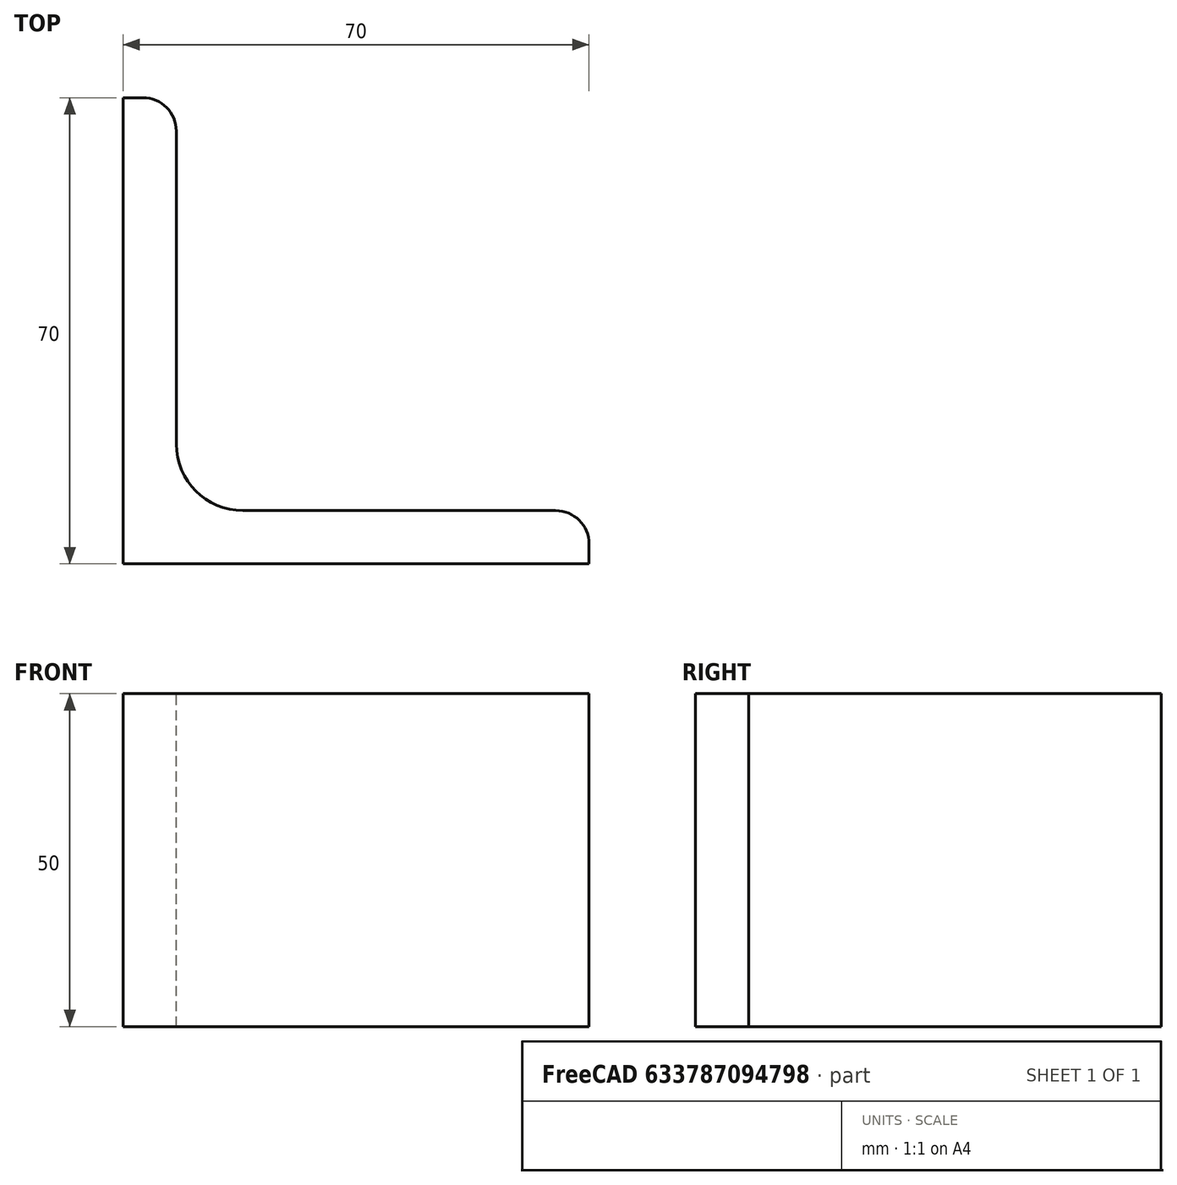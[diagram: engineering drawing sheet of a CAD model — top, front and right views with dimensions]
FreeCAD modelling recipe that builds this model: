
FCSTD DOCUMENT  (FreeCAD 0.15R4671 (Git))
Label: Angle Bar L70x70x8 EN10056 S235JR
License: All rights reserved
LicenseURL: http://en.wikipedia.org/wiki/All_rights_reserved
objects: Sketcher::SketchObject×1, Part::Extrusion×1
note: 2 computed .brp shape members not serialized (recipe doc carries the construction recipe); baked Part::Feature solids carry a one-line shape summary decoded from their .brp

FEATURE [Sketcher::SketchObject] Sketch
  sketch-geometry (9):
    g0: LineSegment StartX=0 StartY=0 StartZ=0 EndX=70 EndY=0 EndZ=0
    g1: LineSegment StartX=70 StartY=0 StartZ=0 EndX=70 EndY=3 EndZ=0
    g2: LineSegment StartX=65 StartY=8 StartZ=0 EndX=18 EndY=8 EndZ=0
    g3: LineSegment StartX=0 StartY=0 StartZ=0 EndX=0 EndY=70 EndZ=0
    g4: LineSegment StartX=0 StartY=70 StartZ=0 EndX=3 EndY=70 EndZ=0
    g5: LineSegment StartX=8 StartY=65 StartZ=0 EndX=8 EndY=18 EndZ=0
    g6: ArcOfCircle CenterX=18 CenterY=18 CenterZ=0 NormalX=0 NormalY=0 NormalZ=1 Radius=10 StartAngle=3.14159 EndAngle=4.71239
    g7: ArcOfCircle CenterX=3 CenterY=65 CenterZ=0 NormalX=0 NormalY=0 NormalZ=1 Radius=5 StartAngle=0 EndAngle=1.5708
    g8: ArcOfCircle CenterX=65 CenterY=3 CenterZ=0 NormalX=0 NormalY=0 NormalZ=1 Radius=5 StartAngle=0 EndAngle=1.5708
  constraints (23):
    c: Coincident(g0,g-1)
    c: Horizontal(g0)
    c: Coincident(g1,g0)
    c: Vertical(g1)
    c: Horizontal(g2)
    c: Coincident(g3,g-1)
    c: Vertical(g3)
    c: Coincident(g4,g3)
    c: Horizontal(g4)
    c: Vertical(g5)
    c: Tangent(g5,g6) = -1.5708
    c: Tangent(g2,g6) = 1.5708
    c: Tangent(g4,g7) = 1.5708
    c: Tangent(g5,g7) = 1.5708
    c: Tangent(g2,g8) = -1.5708
    c: Tangent(g1,g8) = -1.5708
    c: DistanceX(g0) = 70
    c: DistanceY(g3) = 70
    c: DistanceY(g0,g2) = 8
    c: DistanceX(g3,g5) = 8
    c: Radius(g6) = 10
    c: Radius(g8) = 5
    c: Radius(g7) = 5
FEATURE [Part::Extrusion] Extrude  label="Angle Bar L70x70x8 EN10056 S235JR"
  Base = -> Sketch
  Dir = (0,0,50)
  Solid = true
